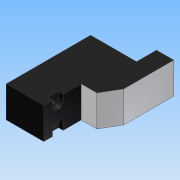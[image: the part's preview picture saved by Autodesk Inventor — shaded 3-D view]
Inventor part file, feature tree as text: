
AUTODESK INVENTOR PART (.ipt)
format: ipt  version: 2012 SP1 (Build 160190100, 190)  size: 140,288 bytes
history: native  units: mm
features: sketch x3, extrude x2, hole x2, mirror x1
ambient origin geometry x8: Origin, YZ Plane, XZ Plane, XY Plane, X Axis, Y Axis, Z Axis, Center Point
bodies: Volumenkörper1 (feature_tree)
feature tree (8):
  extrude  "Extrusion1"  Depth=14.7mm
  hole  "Bohrung1"  [1 undecoded]
  extrude  "Extrusion2"  Depth=5.0mm
  mirror  "Spiegeln1"
  hole  "Bohrung2"  [1 undecoded]
  sketch  "Skizze1"  dims[d0=5.5mm d1=14.7mm]
  sketch  "Skizze2"  dims[d3=12.0mm d4=27.0mm]
  sketch  "Skizze3"  dims[d5=12.0mm d6=5.0mm d7=6.4mm d8=16.0mm d9=10.0mm d10=0.0mm d11=1.75mm d12=4.5mm d13=2.0mm d14=6.0mm d15=3.4mm d16=1.5mm d17=90.0deg d18=8.0mm d19=20.594885mm d20=10.0mm d21=0.0mm d22=2.5mm d23=2.5mm d24=2.8mm d25=7.8mm d26=5.0mm d27=5.3mm d28=1.5mm d29=6.0mm d30=4.0mm d31=2.0mm d32=90.0deg d33=8.0mm d34=20.594885mm d35=0.8mm]
note: 2 required parameter values undecoded (feature->parameter linkage not recoverable at this tier; creation-order binding heuristic only, values carry confidence <= 0.55)
